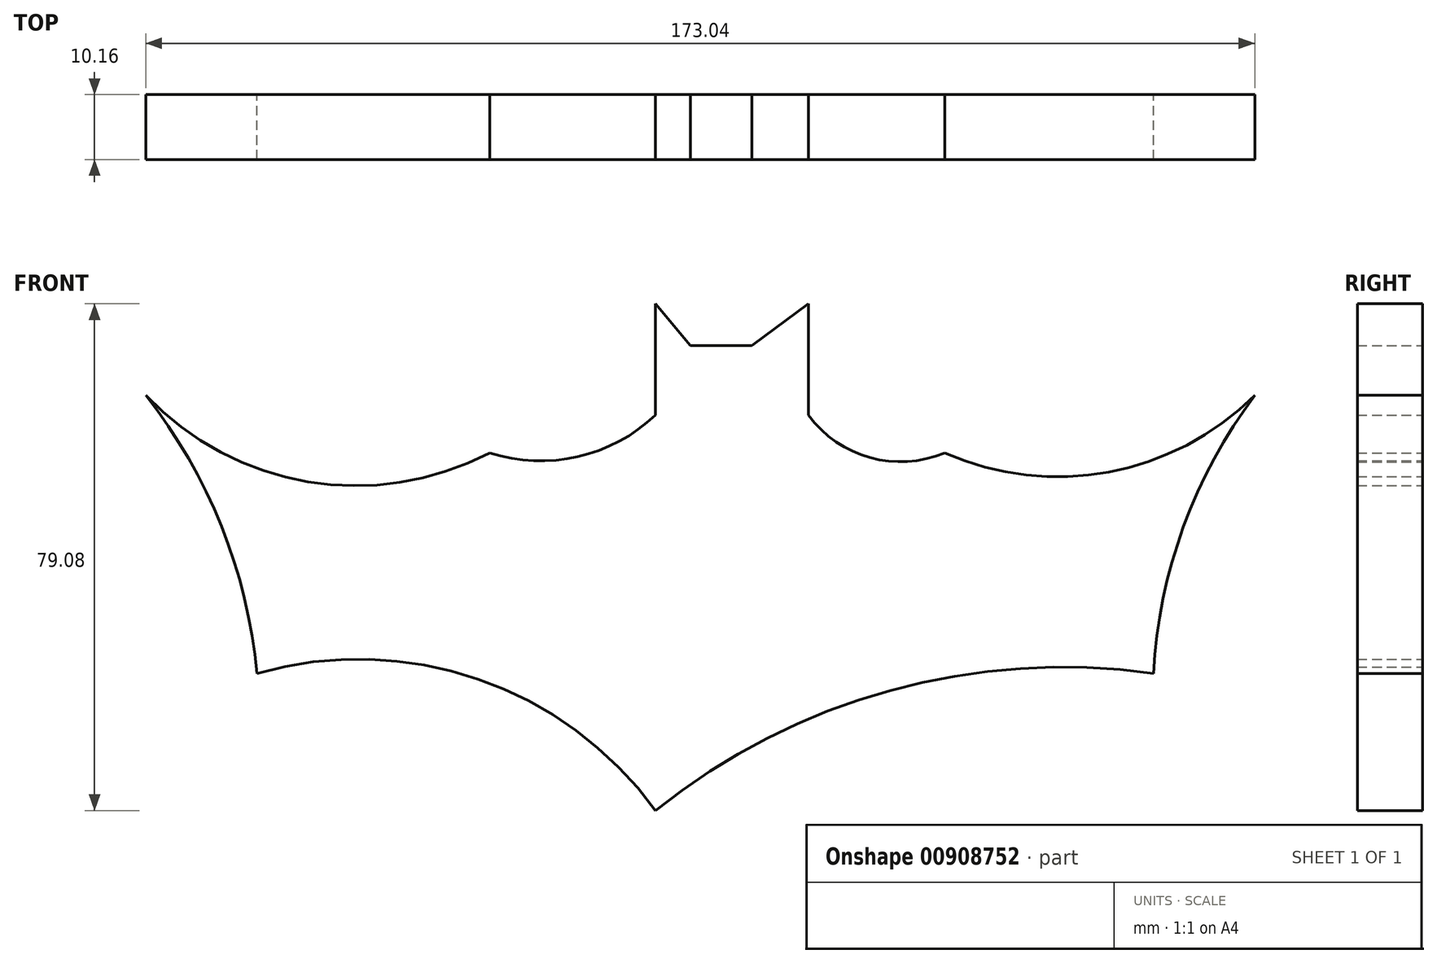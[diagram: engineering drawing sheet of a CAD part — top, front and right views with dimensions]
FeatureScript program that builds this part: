
annotation { "Feature Type Name" : "Feature", "Feature Type Description" : "" }
export const myFeature = defineFeature(function(context is Context, id is Id, definition is map)
    precondition{}
    {
        {
            var Q0;
            Q0=qCreatedBy(makeId("Front.planeOp"),FACE);
            var sketch = newSketch(context, id + "F0", { "sketchPlane" : qUnion([Q0])});
            skArc(sketch, "E0", {"start": v(-79.54, 20) * mm, "mid": v(-54.23, 6.5) * mm, "end": v(-25.9, 11) * mm});
            skArc(sketch, "E1", {"start": v(-62.18, -23.41) * mm, "mid": v(-67.73, -0.45) * mm, "end": v(-79.54, 20) * mm});
            skArc(sketch, "E2", {"start": v(0, -44.81) * mm, "mid": v(-27.71, -24.3) * mm, "end": v(-62.18, -23.41) * mm});
            skArc(sketch, "E3", {"start": v(-25.9, 11) * mm, "mid": v(-12.14, 10.4) * mm, "end": v(0, 16.9) * mm});
            skLineSegment(sketch, "E4", {"start": v(0, 16.9) * mm, "end": v(0, 34.27) * mm});
            skLineSegment(sketch, "E5", {"start": v(0, 34.27) * mm, "end": v(5.43, 27.76) * mm});
            skLineSegment(sketch, "E6", {"start": v(5.43, 27.76) * mm, "end": v(15.04, 27.76) * mm});
            skLineSegment(sketch, "E7", {"start": v(15.04, 27.76) * mm, "end": v(23.86, 34.27) * mm});
            skLineSegment(sketch, "E8", {"start": v(23.86, 34.27) * mm, "end": v(23.86, 16.9) * mm});
            skArc(sketch, "E9", {"start": v(23.86, 16.9) * mm, "mid": v(33.47, 10.26) * mm, "end": v(45.12, 11) * mm});
            skArc(sketch, "E10", {"start": v(45.12, 11) * mm, "mid": v(70.7, 8.02) * mm, "end": v(93.5, 20) * mm});
            skArc(sketch, "E11", {"start": v(93.5, 20) * mm, "mid": v(82.37, -0.53) * mm, "end": v(77.68, -23.41) * mm});
            skArc(sketch, "E12", {"start": v(77.68, -23.41) * mm, "mid": v(36.63, -26.08) * mm, "end": v(0, -44.81) * mm});
            skSolve(sketch);
        }
        {
            var Q0;
            Q0=makeQuery(id+"F0.imprint","IMPRINT",FACE,{"disambiguationData":[TD([[makeQuery(id+"F0.imprint","IMPRINT",EDGE,{"derivedFrom":sQuery(id+"F0.wireOp",EDGE,"E0")}),-1.0]])]});
            extrude(context, id + "F1", {"entities" : qUnion([Q0]), "depth" : 10.16 * mm, "offsetDistance" : 25.4 * mm});
        }
    });
